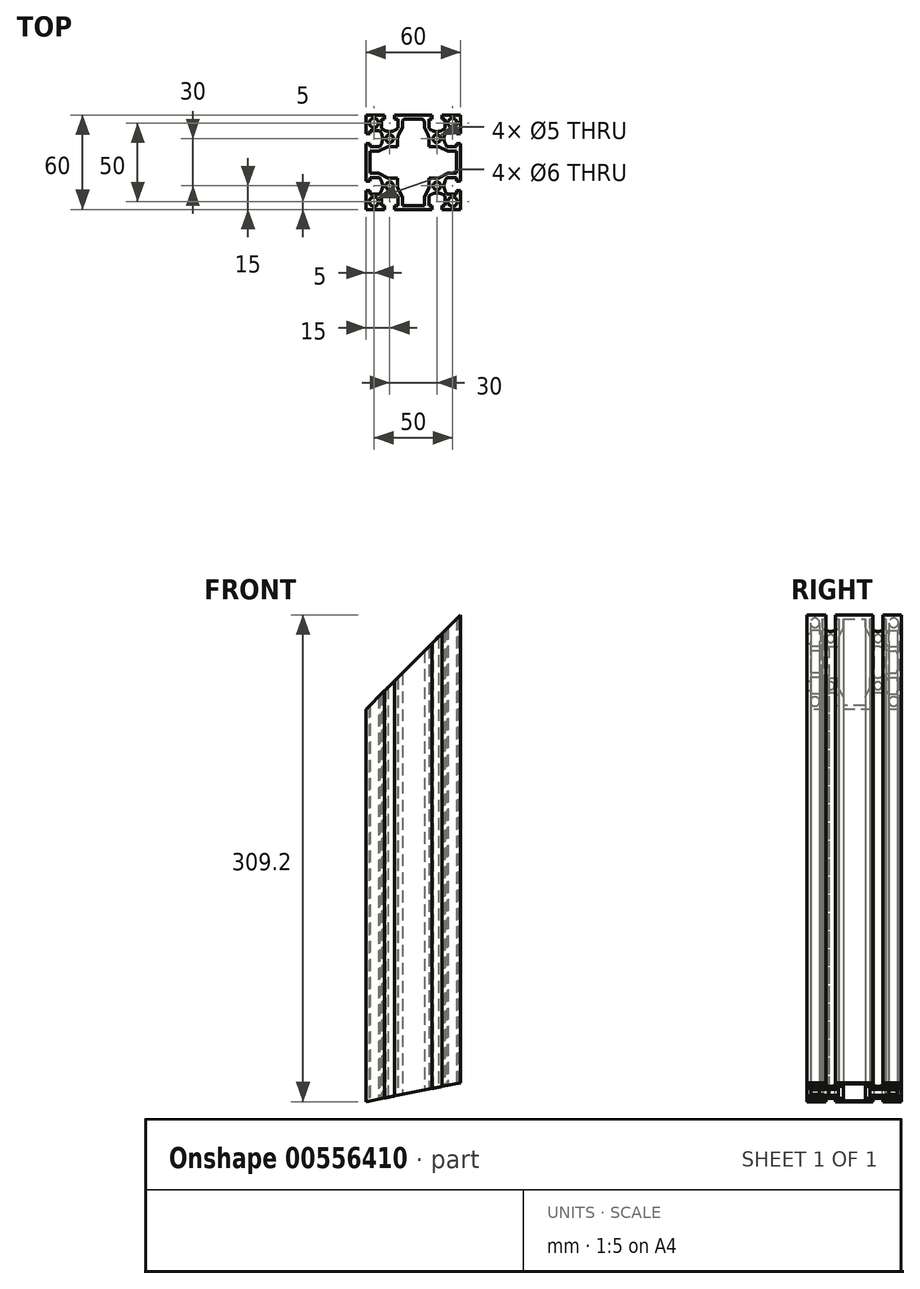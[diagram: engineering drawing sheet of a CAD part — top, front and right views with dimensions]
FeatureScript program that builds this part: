
annotation { "Feature Type Name" : "Feature", "Feature Type Description" : "" }
export const myFeature = defineFeature(function(context is Context, id is Id, definition is map)
    precondition{}
    {
        {
            var Q0;
            Q0=qCreatedBy(makeId("Top.planeOp"),FACE);
            var sketch = newSketch(context, id + "F0", { "sketchPlane" : qUnion([Q0])});
            skLineSegment(sketch, "E0.bottom", {"start": v(30, -30) * mm, "end": v(-30, -30) * mm});
            skLineSegment(sketch, "E0.top", {"start": v(30, 30) * mm, "end": v(-30, 30) * mm});
            skLineSegment(sketch, "E0.left", {"start": v(30, -30) * mm, "end": v(30, 30) * mm});
            skLineSegment(sketch, "E0.right", {"start": v(-30, -30) * mm, "end": v(-30, 30) * mm});
            skPoint(sketch, "E0.middle", {"position": v(0, 0) * mm});
            skLineSegment(sketch, "E1.top", {"start": v(-11.85, 30) * mm, "end": v(-18.15, 30) * mm});
            skLineSegment(sketch, "E1.left", {"start": v(-11.85, 27.5) * mm, "end": v(-11.85, 30) * mm});
            skLineSegment(sketch, "E1.right", {"start": v(-18.15, 27.5) * mm, "end": v(-18.15, 30) * mm});
            skPoint(sketch, "E1.middle", {"position": v(-15, 28.75) * mm});
            skLineSegment(sketch, "E2.bottom", {"start": v(-9.85, 27.5) * mm, "end": v(-11.85, 27.5) * mm});
            skLineSegment(sketch, "E2.left", {"start": v(-9.85, 27.5) * mm, "end": v(-9.85, 21.55) * mm});
            skLineSegment(sketch, "E2.right", {"start": v(-20.15, 27.5) * mm, "end": v(-20.15, 21.55) * mm});
            skPoint(sketch, "E2.middle", {"position": v(-15, 24.52) * mm});
            skArc(sketch, "E3", {"start": v(-20.15, 21.55) * mm, "mid": v(-15, 19.5) * mm, "end": v(-9.85, 21.55) * mm});
            skPoint(sketch, "E4.MirrorP", {"position": v(15, 24.52) * mm});
            skPoint(sketch, "E5.MirrorP", {"position": v(15, 28.75) * mm});
            skLineSegment(sketch, "E6.MirrorCS", {"start": v(11.85, 27.5) * mm, "end": v(11.85, 30) * mm});
            skLineSegment(sketch, "E7.MirrorCS", {"start": v(18.15, 27.5) * mm, "end": v(18.15, 30) * mm});
            skLineSegment(sketch, "E8.MirrorCS", {"start": v(9.85, 27.5) * mm, "end": v(11.85, 27.5) * mm});
            skLineSegment(sketch, "E9.MirrorCS", {"start": v(9.85, 27.5) * mm, "end": v(9.85, 21.55) * mm});
            skArc(sketch, "E10.MirrorCS", {"start": v(20.15, 21.55) * mm, "mid": v(15, 19.5) * mm, "end": v(9.85, 21.55) * mm});
            skLineSegment(sketch, "E11.MirrorCS", {"start": v(20.15, 27.5) * mm, "end": v(20.15, 21.55) * mm});
            skLineSegment(sketch, "E12.MirrorCS", {"start": v(11.85, 30) * mm, "end": v(18.15, 30) * mm});
            skLineSegment(sketch, "E13.1.0", {"start": v(27.5, 20.15) * mm, "end": v(21.55, 20.15) * mm});
            skLineSegment(sketch, "E13.1.1", {"start": v(27.5, 9.85) * mm, "end": v(21.55, 9.85) * mm});
            skArc(sketch, "E13.1.2", {"start": v(21.55, 20.15) * mm, "mid": v(19.5, 15) * mm, "end": v(21.55, 9.85) * mm});
            skLineSegment(sketch, "E13.1.3", {"start": v(27.5, -9.85) * mm, "end": v(21.55, -9.85) * mm});
            skLineSegment(sketch, "E13.1.4", {"start": v(27.5, -20.15) * mm, "end": v(21.55, -20.15) * mm});
            skPoint(sketch, "E13.1.5", {"position": v(28.75, 15) * mm});
            skPoint(sketch, "E13.1.6", {"position": v(28.75, -15) * mm});
            skArc(sketch, "E13.1.7", {"start": v(21.55, -20.15) * mm, "mid": v(19.5, -15) * mm, "end": v(21.55, -9.85) * mm});
            skPoint(sketch, "E13.1.8", {"position": v(24.52, -15) * mm});
            skPoint(sketch, "E13.1.9", {"position": v(24.52, 15) * mm});
            skLineSegment(sketch, "E13.1.10", {"start": v(27.5, 9.85) * mm, "end": v(27.5, 20.15) * mm});
            skLineSegment(sketch, "E13.1.11", {"start": v(27.5, -11.85) * mm, "end": v(27.5, -18.15) * mm});
            skLineSegment(sketch, "E13.1.12", {"start": v(30, 11.85) * mm, "end": v(30, 18.15) * mm});
            skLineSegment(sketch, "E13.1.13", {"start": v(30, -11.85) * mm, "end": v(30, -18.15) * mm});
            skLineSegment(sketch, "E13.1.14", {"start": v(27.5, 18.15) * mm, "end": v(30, 18.15) * mm});
            skLineSegment(sketch, "E13.1.15", {"start": v(27.5, 11.85) * mm, "end": v(30, 11.85) * mm});
            skLineSegment(sketch, "E13.1.16", {"start": v(27.5, 11.85) * mm, "end": v(27.5, 18.15) * mm});
            skLineSegment(sketch, "E13.1.17", {"start": v(27.5, -9.85) * mm, "end": v(27.5, -20.15) * mm});
            skLineSegment(sketch, "E13.1.18", {"start": v(27.5, -18.15) * mm, "end": v(30, -18.15) * mm});
            skLineSegment(sketch, "E13.1.19", {"start": v(27.5, -11.85) * mm, "end": v(30, -11.85) * mm});
            skLineSegment(sketch, "E13.2.0", {"start": v(20.15, -27.5) * mm, "end": v(20.15, -21.55) * mm});
            skLineSegment(sketch, "E13.2.1", {"start": v(9.85, -27.5) * mm, "end": v(9.85, -21.55) * mm});
            skArc(sketch, "E13.2.2", {"start": v(20.15, -21.55) * mm, "mid": v(15, -19.5) * mm, "end": v(9.85, -21.55) * mm});
            skLineSegment(sketch, "E13.2.3", {"start": v(-9.85, -27.5) * mm, "end": v(-9.85, -21.55) * mm});
            skLineSegment(sketch, "E13.2.4", {"start": v(-20.15, -27.5) * mm, "end": v(-20.15, -21.55) * mm});
            skPoint(sketch, "E13.2.5", {"position": v(15, -28.75) * mm});
            skPoint(sketch, "E13.2.6", {"position": v(-15, -28.75) * mm});
            skArc(sketch, "E13.2.7", {"start": v(-20.15, -21.55) * mm, "mid": v(-15, -19.5) * mm, "end": v(-9.85, -21.55) * mm});
            skPoint(sketch, "E13.2.8", {"position": v(-15, -24.52) * mm});
            skPoint(sketch, "E13.2.9", {"position": v(15, -24.52) * mm});
            skLineSegment(sketch, "E13.2.10", {"start": v(9.85, -27.5) * mm, "end": v(20.15, -27.5) * mm});
            skLineSegment(sketch, "E13.2.11", {"start": v(-11.85, -27.5) * mm, "end": v(-18.15, -27.5) * mm});
            skLineSegment(sketch, "E13.2.12", {"start": v(11.85, -30) * mm, "end": v(18.15, -30) * mm});
            skLineSegment(sketch, "E13.2.13", {"start": v(-11.85, -30) * mm, "end": v(-18.15, -30) * mm});
            skLineSegment(sketch, "E13.2.14", {"start": v(18.15, -27.5) * mm, "end": v(18.15, -30) * mm});
            skLineSegment(sketch, "E13.2.15", {"start": v(11.85, -27.5) * mm, "end": v(11.85, -30) * mm});
            skLineSegment(sketch, "E13.2.16", {"start": v(11.85, -27.5) * mm, "end": v(18.15, -27.5) * mm});
            skLineSegment(sketch, "E13.2.17", {"start": v(-9.85, -27.5) * mm, "end": v(-20.15, -27.5) * mm});
            skLineSegment(sketch, "E13.2.18", {"start": v(-18.15, -27.5) * mm, "end": v(-18.15, -30) * mm});
            skLineSegment(sketch, "E13.2.19", {"start": v(-11.85, -27.5) * mm, "end": v(-11.85, -30) * mm});
            skLineSegment(sketch, "E13.3.0", {"start": v(-27.5, -20.15) * mm, "end": v(-21.55, -20.15) * mm});
            skLineSegment(sketch, "E13.3.1", {"start": v(-27.5, -9.85) * mm, "end": v(-21.55, -9.85) * mm});
            skArc(sketch, "E13.3.2", {"start": v(-21.55, -20.15) * mm, "mid": v(-19.5, -15) * mm, "end": v(-21.55, -9.85) * mm});
            skLineSegment(sketch, "E13.3.3", {"start": v(-27.5, 9.85) * mm, "end": v(-21.55, 9.85) * mm});
            skLineSegment(sketch, "E13.3.4", {"start": v(-27.5, 20.15) * mm, "end": v(-21.55, 20.15) * mm});
            skPoint(sketch, "E13.3.5", {"position": v(-28.75, -15) * mm});
            skPoint(sketch, "E13.3.6", {"position": v(-28.75, 15) * mm});
            skArc(sketch, "E13.3.7", {"start": v(-21.55, 20.15) * mm, "mid": v(-19.5, 15) * mm, "end": v(-21.55, 9.85) * mm});
            skPoint(sketch, "E13.3.8", {"position": v(-24.52, 15) * mm});
            skPoint(sketch, "E13.3.9", {"position": v(-24.52, -15) * mm});
            skLineSegment(sketch, "E13.3.10", {"start": v(-27.5, -9.85) * mm, "end": v(-27.5, -20.15) * mm});
            skLineSegment(sketch, "E13.3.11", {"start": v(-27.5, 11.85) * mm, "end": v(-27.5, 18.15) * mm});
            skLineSegment(sketch, "E13.3.12", {"start": v(-30, -11.85) * mm, "end": v(-30, -18.15) * mm});
            skLineSegment(sketch, "E13.3.13", {"start": v(-30, 11.85) * mm, "end": v(-30, 18.15) * mm});
            skLineSegment(sketch, "E13.3.14", {"start": v(-27.5, -18.15) * mm, "end": v(-30, -18.15) * mm});
            skLineSegment(sketch, "E13.3.15", {"start": v(-27.5, -11.85) * mm, "end": v(-30, -11.85) * mm});
            skLineSegment(sketch, "E13.3.16", {"start": v(-27.5, -11.85) * mm, "end": v(-27.5, -18.15) * mm});
            skLineSegment(sketch, "E13.3.17", {"start": v(-27.5, 9.85) * mm, "end": v(-27.5, 20.15) * mm});
            skLineSegment(sketch, "E13.3.18", {"start": v(-27.5, 18.15) * mm, "end": v(-30, 18.15) * mm});
            skLineSegment(sketch, "E13.3.19", {"start": v(-27.5, 11.85) * mm, "end": v(-30, 11.85) * mm});
            skLineSegment(sketch, "E13.anchor1", {"start": v(0, 0) * mm, "end": v(-20.15, 21.55) * mm, "construction": true});
            skLineSegment(sketch, "E13.anchor2", {"start": v(0, 0) * mm, "end": v(-21.55, -20.15) * mm, "construction": true});
            skLineSegment(sketch, "E14.trimOffspring", {"start": v(-18.15, 27.5) * mm, "end": v(-20.15, 27.5) * mm});
            skLineSegment(sketch, "E15.trimOffspring", {"start": v(18.15, 27.5) * mm, "end": v(20.15, 27.5) * mm});
            skCircle(sketch, "E16", {"center": v(-15, 15) * mm, "radius": 2.5 * mm});
            skCircle(sketch, "E17", {"center": v(-25, 25) * mm, "radius": 3 * mm});
            skCircle(sketch, "E18.MirrorC", {"center": v(25, 25) * mm, "radius": 3 * mm});
            skCircle(sketch, "E19.MirrorC", {"center": v(25, -25) * mm, "radius": 3 * mm});
            skCircle(sketch, "E20.MirrorC", {"center": v(-25, -25) * mm, "radius": 3 * mm});
            skCircle(sketch, "E21.MirrorC", {"center": v(15, 15) * mm, "radius": 2.5 * mm});
            skCircle(sketch, "E22.MirrorC", {"center": v(15, -15) * mm, "radius": 2.5 * mm});
            skCircle(sketch, "E23.MirrorC", {"center": v(-15, -15) * mm, "radius": 2.5 * mm});
            skLineSegment(sketch, "E24", {"start": v(-7, 27.5) * mm, "end": v(0, 27.5) * mm});
            skLineSegment(sketch, "E25", {"start": v(-7, 27.5) * mm, "end": v(-7, 22) * mm});
            skLineSegment(sketch, "E26", {"start": v(-10, 10) * mm, "end": v(-10, 16) * mm});
            skLineSegment(sketch, "E27", {"start": v(-10, 16) * mm, "end": v(-7, 22) * mm});
            skLineSegment(sketch, "E28.MirrorCS", {"start": v(10, 10) * mm, "end": v(10, 16) * mm});
            skLineSegment(sketch, "E29.MirrorCS", {"start": v(10, 16) * mm, "end": v(7, 22) * mm});
            skLineSegment(sketch, "E30.MirrorCS", {"start": v(7, 27.5) * mm, "end": v(0, 27.5) * mm});
            skLineSegment(sketch, "E31.MirrorCS", {"start": v(7, 27.5) * mm, "end": v(7, 22) * mm});
            skLineSegment(sketch, "E32.1.0", {"start": v(-10, -10) * mm, "end": v(-16, -10) * mm});
            skLineSegment(sketch, "E32.1.1", {"start": v(-16, -10) * mm, "end": v(-22, -7) * mm});
            skLineSegment(sketch, "E32.1.2", {"start": v(-27.5, -7) * mm, "end": v(-22, -7) * mm});
            skLineSegment(sketch, "E32.1.3", {"start": v(-27.5, -7) * mm, "end": v(-27.5, 0) * mm});
            skLineSegment(sketch, "E32.1.4", {"start": v(-27.5, 7) * mm, "end": v(-27.5, 0) * mm});
            skLineSegment(sketch, "E32.1.5", {"start": v(-27.5, 7) * mm, "end": v(-22, 7) * mm});
            skLineSegment(sketch, "E32.1.6", {"start": v(-16, 10) * mm, "end": v(-22, 7) * mm});
            skLineSegment(sketch, "E32.1.7", {"start": v(-10, 10) * mm, "end": v(-16, 10) * mm});
            skLineSegment(sketch, "E32.2.0", {"start": v(10, -10) * mm, "end": v(10, -16) * mm});
            skLineSegment(sketch, "E32.2.1", {"start": v(10, -16) * mm, "end": v(7, -22) * mm});
            skLineSegment(sketch, "E32.2.2", {"start": v(7, -27.5) * mm, "end": v(7, -22) * mm});
            skLineSegment(sketch, "E32.2.3", {"start": v(7, -27.5) * mm, "end": v(0, -27.5) * mm});
            skLineSegment(sketch, "E32.2.4", {"start": v(-7, -27.5) * mm, "end": v(0, -27.5) * mm});
            skLineSegment(sketch, "E32.2.5", {"start": v(-7, -27.5) * mm, "end": v(-7, -22) * mm});
            skLineSegment(sketch, "E32.2.6", {"start": v(-10, -16) * mm, "end": v(-7, -22) * mm});
            skLineSegment(sketch, "E32.2.7", {"start": v(-10, -10) * mm, "end": v(-10, -16) * mm});
            skLineSegment(sketch, "E32.3.0", {"start": v(10, 10) * mm, "end": v(16, 10) * mm});
            skLineSegment(sketch, "E32.3.1", {"start": v(16, 10) * mm, "end": v(22, 7) * mm});
            skLineSegment(sketch, "E32.3.2", {"start": v(27.5, 7) * mm, "end": v(22, 7) * mm});
            skLineSegment(sketch, "E32.3.3", {"start": v(27.5, 7) * mm, "end": v(27.5, 0) * mm});
            skLineSegment(sketch, "E32.3.4", {"start": v(27.5, -7) * mm, "end": v(27.5, 0) * mm});
            skLineSegment(sketch, "E32.3.5", {"start": v(27.5, -7) * mm, "end": v(22, -7) * mm});
            skLineSegment(sketch, "E32.3.6", {"start": v(16, -10) * mm, "end": v(22, -7) * mm});
            skLineSegment(sketch, "E32.3.7", {"start": v(10, -10) * mm, "end": v(16, -10) * mm});
            skSolve(sketch);
        }
        {
            var Q0;
            {var subQ30=sQuery(id+"F0.wireOp",EDGE,"E1.left");Q0=makeQuery(id+"F0.imprint","IMPRINT",FACE,{"disambiguationData":[TD([[makeQuery(id+"F0.imprint","IMPRINT",EDGE,{"derivedFrom":subQ30}),-1.0]])]});}
            extrude(context, id + "F1", {"entities" : qUnion([Q0]), "depth" : 309.2 * mm, "offsetDistance" : 25 * mm});
        }
        {
            var Q0;
            Q0=makeQuery(id+"F1.opExtrude","SWEPT_EDGE",EDGE,{"disambiguationData":[OSD([sQuery(id+"F0.wireOp",EDGE,"E24"),sQuery(id+"F0.wireOp",EDGE,"E25")])]});
            var Q1;
            Q1=makeQuery(id+"F1.opExtrude","SWEPT_EDGE",EDGE,{"disambiguationData":[OSD([sQuery(id+"F0.wireOp",EDGE,"E30.MirrorCS"),sQuery(id+"F0.wireOp",EDGE,"E31.MirrorCS")])]});
            var Q2;
            Q2=makeQuery(id+"F1.opExtrude","SWEPT_EDGE",EDGE,{"disambiguationData":[OSD([sQuery(id+"F0.wireOp",EDGE,"840db5bc-c403-45cd-90c7-254e62d9e8c5.3.2"),sQuery(id+"F0.wireOp",EDGE,"840db5bc-c403-45cd-90c7-254e62d9e8c5.3.3")])]});
            var Q3;
            Q3=makeQuery(id+"F1.opExtrude","SWEPT_EDGE",EDGE,{"disambiguationData":[OSD([sQuery(id+"F0.wireOp",EDGE,"840db5bc-c403-45cd-90c7-254e62d9e8c5.3.4"),sQuery(id+"F0.wireOp",EDGE,"840db5bc-c403-45cd-90c7-254e62d9e8c5.3.5")])]});
            var Q4;
            Q4=makeQuery(id+"F1.opExtrude","SWEPT_EDGE",EDGE,{"disambiguationData":[OSD([sQuery(id+"F0.wireOp",EDGE,"840db5bc-c403-45cd-90c7-254e62d9e8c5.1.4"),sQuery(id+"F0.wireOp",EDGE,"840db5bc-c403-45cd-90c7-254e62d9e8c5.1.5")])]});
            var Q5;
            Q5=makeQuery(id+"F1.opExtrude","SWEPT_EDGE",EDGE,{"disambiguationData":[OSD([sQuery(id+"F0.wireOp",EDGE,"840db5bc-c403-45cd-90c7-254e62d9e8c5.1.2"),sQuery(id+"F0.wireOp",EDGE,"840db5bc-c403-45cd-90c7-254e62d9e8c5.1.3")])]});
            var Q6;
            Q6=makeQuery(id+"F1.opExtrude","SWEPT_EDGE",EDGE,{"disambiguationData":[OSD([sQuery(id+"F0.wireOp",EDGE,"840db5bc-c403-45cd-90c7-254e62d9e8c5.2.2"),sQuery(id+"F0.wireOp",EDGE,"840db5bc-c403-45cd-90c7-254e62d9e8c5.2.3")])]});
            var Q7;
            Q7=makeQuery(id+"F1.opExtrude","SWEPT_EDGE",EDGE,{"disambiguationData":[OSD([sQuery(id+"F0.wireOp",EDGE,"840db5bc-c403-45cd-90c7-254e62d9e8c5.2.4"),sQuery(id+"F0.wireOp",EDGE,"840db5bc-c403-45cd-90c7-254e62d9e8c5.2.5")])]});
            fillet(context, id + "F2", {"entities" : qUnion([Q0, Q1, Q2, Q3, Q4, Q5, Q6, Q7]), "radius" : 2 * mm, "tangentPropagation" : true, "allowEdgeOverflow" : false});
        }
        {
            var Q0;
            Q0=makeQuery(id+"F1.opExtrude","SWEPT_EDGE",EDGE,{"disambiguationData":[OSD([sQuery(id+"F0.wireOp",EDGE,"E26"),sQuery(id+"F0.wireOp",EDGE,"E27")])]});
            var Q1;
            Q1=makeQuery(id+"F1.opExtrude","SWEPT_EDGE",EDGE,{"disambiguationData":[OSD([sQuery(id+"F0.wireOp",EDGE,"E28.MirrorCS"),sQuery(id+"F0.wireOp",EDGE,"E29.MirrorCS")])]});
            var Q2;
            Q2=makeQuery(id+"F1.opExtrude","SWEPT_EDGE",EDGE,{"disambiguationData":[OSD([sQuery(id+"F0.wireOp",EDGE,"840db5bc-c403-45cd-90c7-254e62d9e8c5.3.0"),sQuery(id+"F0.wireOp",EDGE,"840db5bc-c403-45cd-90c7-254e62d9e8c5.3.1")])]});
            var Q3;
            Q3=makeQuery(id+"F1.opExtrude","SWEPT_EDGE",EDGE,{"disambiguationData":[OSD([sQuery(id+"F0.wireOp",EDGE,"840db5bc-c403-45cd-90c7-254e62d9e8c5.1.6"),sQuery(id+"F0.wireOp",EDGE,"840db5bc-c403-45cd-90c7-254e62d9e8c5.1.7")])]});
            var Q4;
            Q4=makeQuery(id+"F1.opExtrude","SWEPT_EDGE",EDGE,{"disambiguationData":[OSD([sQuery(id+"F0.wireOp",EDGE,"840db5bc-c403-45cd-90c7-254e62d9e8c5.1.0"),sQuery(id+"F0.wireOp",EDGE,"840db5bc-c403-45cd-90c7-254e62d9e8c5.1.1")])]});
            var Q5;
            Q5=makeQuery(id+"F1.opExtrude","SWEPT_EDGE",EDGE,{"disambiguationData":[OSD([sQuery(id+"F0.wireOp",EDGE,"840db5bc-c403-45cd-90c7-254e62d9e8c5.3.6"),sQuery(id+"F0.wireOp",EDGE,"840db5bc-c403-45cd-90c7-254e62d9e8c5.3.7")])]});
            var Q6;
            Q6=makeQuery(id+"F1.opExtrude","SWEPT_EDGE",EDGE,{"disambiguationData":[OSD([sQuery(id+"F0.wireOp",EDGE,"840db5bc-c403-45cd-90c7-254e62d9e8c5.2.0"),sQuery(id+"F0.wireOp",EDGE,"840db5bc-c403-45cd-90c7-254e62d9e8c5.2.1")])]});
            var Q7;
            Q7=makeQuery(id+"F1.opExtrude","SWEPT_EDGE",EDGE,{"disambiguationData":[OSD([sQuery(id+"F0.wireOp",EDGE,"840db5bc-c403-45cd-90c7-254e62d9e8c5.2.6"),sQuery(id+"F0.wireOp",EDGE,"840db5bc-c403-45cd-90c7-254e62d9e8c5.2.7")])]});
            fillet(context, id + "F3", {"entities" : qUnion([Q0, Q1, Q2, Q3, Q4, Q5, Q6, Q7]), "radius" : 7 * mm, "tangentPropagation" : true, "allowEdgeOverflow" : false});
        }
        {
            var Q0;
            {var subQ0=sQuery(id+"F0.wireOp",EDGE,"E0.bottom");Q0=makeQuery(id+"F1.opExtrude","SWEPT_FACE",FACE,{"disambiguationData":[OSD([subQ0]),TDD([makeQuery(id+"F0.imprint","IMPRINT",EDGE,{"disambiguationData":[TD([[makeQuery(id+"F0.imprint","INTERSECT",VERTEX,{"derivedFrom":[subQ0,sQuery(id+"F0.wireOp",EDGE,"E13.2.12"),sQuery(id+"F0.wireOp",EDGE,"E13.2.15")]}),-1.0]])],"derivedFrom":subQ0})])]});}
            var sketch = newSketch(context, id + "F4", { "sketchPlane" : qUnion([Q0])});
            skLineSegment(sketch, "E33.0", {"start": v(-18.15, 309.2) * mm, "end": v(-30, 309.2) * mm});
            skLineSegment(sketch, "E33.1", {"start": v(30, 309.2) * mm, "end": v(30, 0) * mm});
            skLineSegment(sketch, "E34", {"start": v(-30, 309.2) * mm, "end": v(30, 309.2) * mm});
            skLineSegment(sketch, "E35", {"start": v(30, 249.2) * mm, "end": v(-30, 309.2) * mm});
            skLineSegment(sketch, "E36.0", {"start": v(-18.15, 0) * mm, "end": v(-30, 0) * mm});
            skLineSegment(sketch, "E37", {"start": v(-30, 0) * mm, "end": v(30, 0) * mm});
            skLineSegment(sketch, "E38", {"start": v(30, 60) * mm, "end": v(-30, 0) * mm});
            skSolve(sketch);
        }
        {
            var Q0;
            Q0=qCreatedBy(makeId("Front.planeOp"),FACE);
            var sketch = newSketch(context, id + "F5", { "sketchPlane" : qUnion([Q0])});
            skLineSegment(sketch, "E39.bottom", {"start": v(175.88, 40.95) * mm, "end": v(-30, 0) * mm});
            skLineSegment(sketch, "E39.top", {"start": v(199.67, -78.65) * mm, "end": v(-6.2, -119.6) * mm});
            skLineSegment(sketch, "E39.left", {"start": v(175.88, 40.95) * mm, "end": v(199.67, -78.65) * mm});
            skLineSegment(sketch, "E39.right", {"start": v(-30, 0) * mm, "end": v(-6.2, -119.6) * mm});
            skLineSegment(sketch, "E40.bottom", {"start": v(-52.07, 391.27) * mm, "end": v(-206.7, 236.66) * mm});
            skLineSegment(sketch, "E40.top", {"start": v(30, 309.2) * mm, "end": v(-124.62, 154.58) * mm});
            skLineSegment(sketch, "E40.left", {"start": v(-52.07, 391.27) * mm, "end": v(30, 309.2) * mm});
            skLineSegment(sketch, "E40.right", {"start": v(-206.7, 236.66) * mm, "end": v(-124.62, 154.58) * mm});
            skSolve(sketch);
        }
        {
            var Q0;
            Q0=qSketchRegion(id+"F5",true);
            extrude(context, id + "F6", {"entities" : qUnion([Q0]), "operationType" : NewBodyOperationType.REMOVE, "depth" : 30 * mm, "offsetDistance" : 25 * mm, "hasSecondDirection" : true, "secondDirectionOppositeDirection" : true, "secondDirectionDepth" : 30 * mm});
        }
    });
